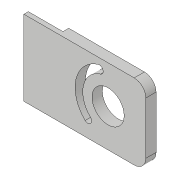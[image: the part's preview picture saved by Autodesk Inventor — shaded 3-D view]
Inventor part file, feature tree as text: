
AUTODESK INVENTOR PART (.ipt)
format: ipt  version: 2018.3 (Build 223284000, 284)  size: 129,536 bytes
history: native  units: in
note: dims shown in document units (in); Inventor stores cm internally (conversion verified against a paired STEP export)
features: extrude x2, sketch x2, fillet x1
ambient origin geometry x8: Origin, YZ Plane, XZ Plane, XY Plane, X Axis, Y Axis, Z Axis, Center Point
bodies: Solid1 (feature_tree)
feature tree (5):
  extrude  "Extrusion1"  Depth=0.221in TaperAngle=0.0deg
  extrude  "Extrusion5"  Depth=0.082in
  fillet  "Fillet1"  Radius=1.25in
  sketch  "Sketch1"  dims[d0=1.625in d1=2.625in d4=0.6925in d5=0.8125in d8=0.221in d9=0.0in]
  sketch  "Sketch5"  dims[d22=0.8125in d23=1.0in d24=1.25in d37=0.119in d38=0.625in d39=0.125in d40=0.125in d41=0.0in d42=0.25in d43=0.0625in d44=0.085in d54=0.082in d55=0.628in]
